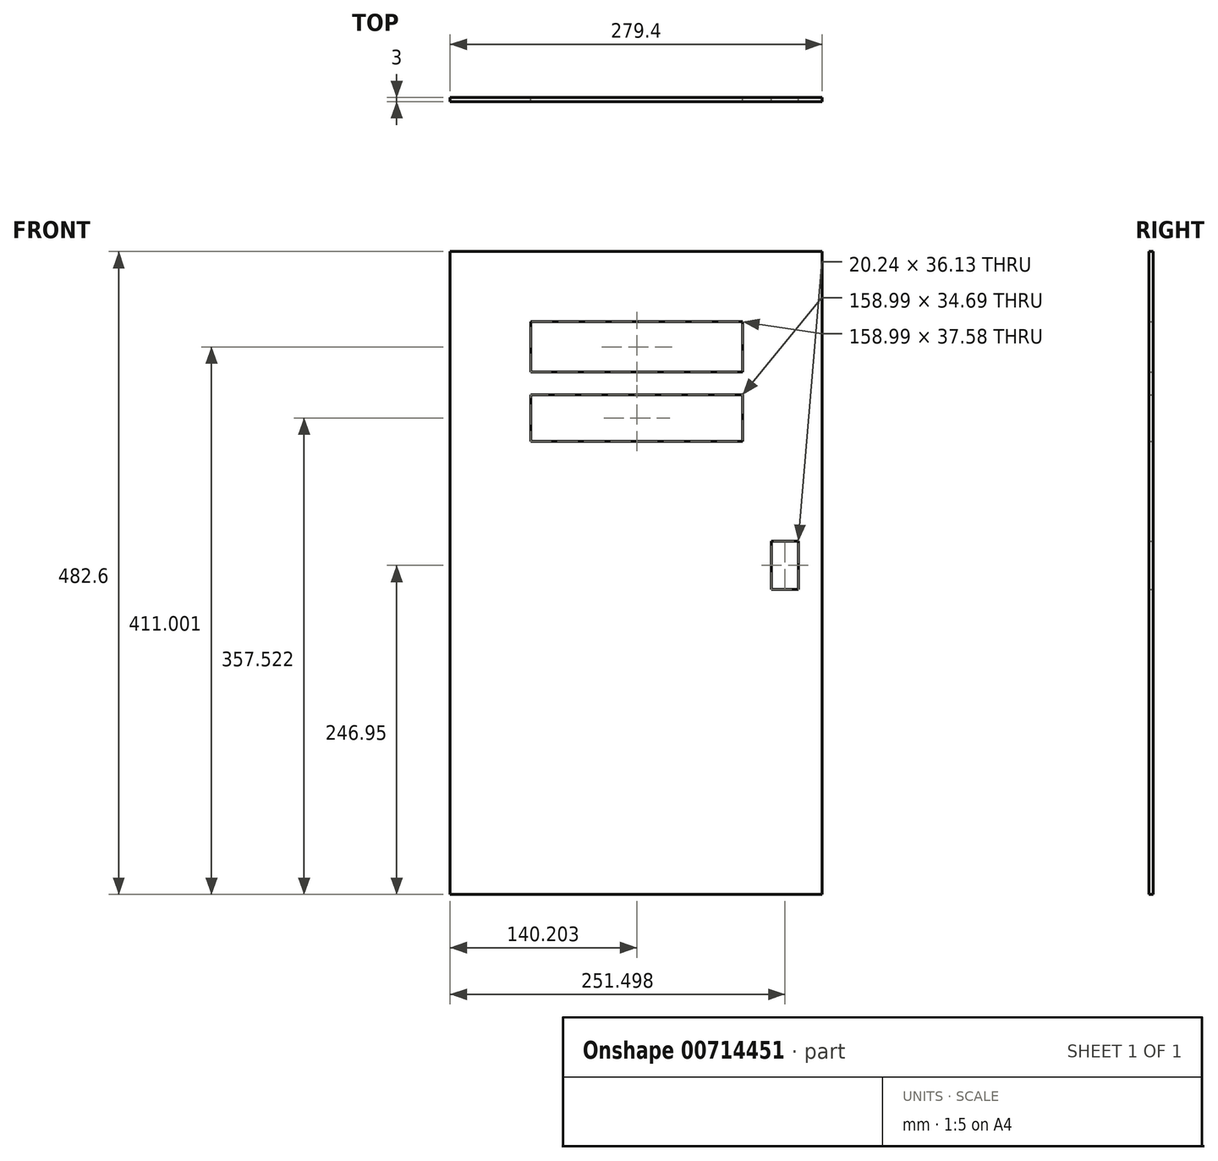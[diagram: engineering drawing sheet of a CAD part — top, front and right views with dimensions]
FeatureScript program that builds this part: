
annotation { "Feature Type Name" : "Feature", "Feature Type Description" : "" }
export const myFeature = defineFeature(function(context is Context, id is Id, definition is map)
    precondition{}
    {
        {
            var Q0;
            Q0=qCreatedBy(makeId("Front.planeOp"),FACE);
            var sketch = newSketch(context, id + "F0", { "sketchPlane" : qUnion([Q0])});
            skLineSegment(sketch, "E0.bottom", {"start": v(-139.7, 241.3) * mm, "end": v(139.7, 241.3) * mm});
            skLineSegment(sketch, "E0.top", {"start": v(-139.7, -241.3) * mm, "end": v(139.7, -241.3) * mm});
            skLineSegment(sketch, "E0.left", {"start": v(-139.7, 241.3) * mm, "end": v(-139.7, -241.3) * mm});
            skLineSegment(sketch, "E0.right", {"start": v(139.7, 241.3) * mm, "end": v(139.7, -241.3) * mm});
            skPoint(sketch, "E0.middle", {"position": v(0, 0) * mm});
            skLineSegment(sketch, "E1.bottom", {"start": v(-79, 188.5) * mm, "end": v(80, 188.5) * mm});
            skLineSegment(sketch, "E1.top", {"start": v(-79, 150.91) * mm, "end": v(80, 150.91) * mm});
            skLineSegment(sketch, "E1.left", {"start": v(-79, 188.5) * mm, "end": v(-79, 150.91) * mm});
            skLineSegment(sketch, "E1.right", {"start": v(80, 188.5) * mm, "end": v(80, 150.91) * mm});
            skLineSegment(sketch, "E2.bottom", {"start": v(-79, 133.57) * mm, "end": v(80, 133.57) * mm});
            skLineSegment(sketch, "E2.top", {"start": v(-79, 98.88) * mm, "end": v(80, 98.88) * mm});
            skLineSegment(sketch, "E2.left", {"start": v(-79, 133.57) * mm, "end": v(-79, 98.88) * mm});
            skLineSegment(sketch, "E2.right", {"start": v(80, 133.57) * mm, "end": v(80, 98.88) * mm});
            skLineSegment(sketch, "E3.bottom", {"start": v(101.68, 23.72) * mm, "end": v(121.92, 23.72) * mm});
            skLineSegment(sketch, "E3.top", {"start": v(101.68, -12.42) * mm, "end": v(121.92, -12.42) * mm});
            skLineSegment(sketch, "E3.left", {"start": v(101.68, 23.72) * mm, "end": v(101.68, -12.42) * mm});
            skLineSegment(sketch, "E3.right", {"start": v(121.92, 23.72) * mm, "end": v(121.92, -12.42) * mm});
            skSolve(sketch);
        }
        {
            var Q0;
            Q0 = qSketchRegion(id + "F0", true);
            extrude(context, id + "F1", {"entities" : qUnion([Q0]), "depth" : 3 * mm, "offsetDistance" : 25.4 * mm});
        }
    });
